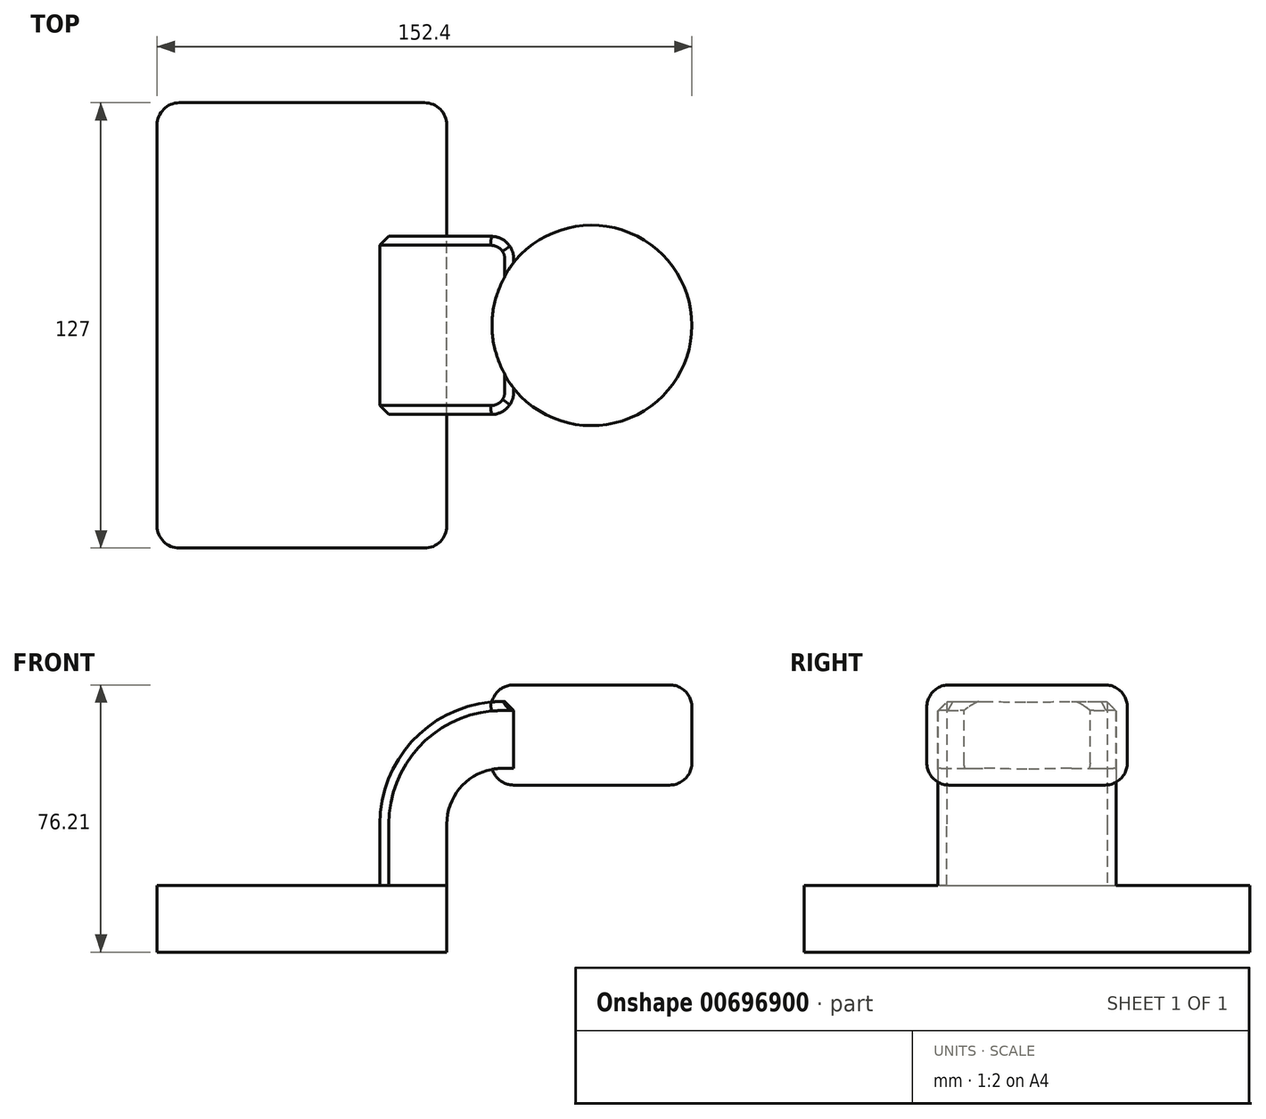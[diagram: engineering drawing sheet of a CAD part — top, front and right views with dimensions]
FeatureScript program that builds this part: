
annotation { "Feature Type Name" : "Feature", "Feature Type Description" : "" }
export const myFeature = defineFeature(function(context is Context, id is Id, definition is map)
    precondition{}
    {
        {
            var Q0;
            Q0=qCreatedBy(makeId("Front.planeOp"),FACE);
            var sketch = newSketch(context, id + "F0", { "sketchPlane" : qUnion([Q0])});
            skLineSegment(sketch, "E0.bottom", {"start": v(-41.28, 9.52) * mm, "end": v(41.27, 9.53) * mm});
            skLineSegment(sketch, "E0.top", {"start": v(-41.28, -9.52) * mm, "end": v(41.28, -9.52) * mm});
            skLineSegment(sketch, "E0.left", {"start": v(-41.28, 9.52) * mm, "end": v(-41.28, -9.53) * mm});
            skLineSegment(sketch, "E0.right", {"start": v(41.27, 9.53) * mm, "end": v(41.28, -9.52) * mm});
            skPoint(sketch, "E0.middle", {"position": v(0, 0) * mm});
            skLineSegment(sketch, "E1.bottom", {"start": v(111.12, 38.1) * mm, "end": v(60.32, 38.1) * mm});
            skLineSegment(sketch, "E1.top", {"start": v(111.12, 66.68) * mm, "end": v(60.32, 66.68) * mm});
            skLineSegment(sketch, "E1.left", {"start": v(111.12, 38.1) * mm, "end": v(111.12, 66.68) * mm});
            skLineSegment(sketch, "E1.right", {"start": v(60.32, 38.1) * mm, "end": v(60.32, 66.68) * mm});
            skPoint(sketch, "E1.middle", {"position": v(85.72, 52.39) * mm});
            skLineSegment(sketch, "E2", {"start": v(41.27, 9.53) * mm, "end": v(41.27, 27) * mm});
            skArc(sketch, "E3", {"start": v(41.27, 27) * mm, "mid": v(45.92, 38.23) * mm, "end": v(57.15, 42.88) * mm});
            skLineSegment(sketch, "E4", {"start": v(57.15, 42.88) * mm, "end": v(82.55, 42.88) * mm});
            skLineSegment(sketch, "E5.0", {"start": v(57.15, 61.93) * mm, "end": v(82.55, 61.93) * mm});
            skArc(sketch, "E5.1", {"start": v(22.22, 27) * mm, "mid": v(32.45, 51.7) * mm, "end": v(57.15, 61.93) * mm});
            skLineSegment(sketch, "E5.2", {"start": v(22.22, 9.53) * mm, "end": v(22.22, 27) * mm});
            skFitSpline(sketch, "E6", {"points": [v(-41.28, 9.52) * mm, v(57.15, 61.93) * mm], "startDerivative": vector(-0.04, 87.73) * mm, "endDerivative": vector(126.82, -4.98) * mm});
            skLineSegment(sketch, "E7", {"start": v(82.55, 66.68) * mm, "end": v(82.55, 38.1) * mm});
            skSolve(sketch);
        }
        {
            var Q0;
            Q0=makeQuery(id+"F0.imprint","IMPRINT",FACE,{"disambiguationData":[TD([[makeQuery(id+"F0.imprint","IMPRINT",EDGE,{"derivedFrom":sQuery(id+"F0.wireOp",EDGE,"E0.top")}),1.0]])]});
            extrude(context, id + "F1", {"entities" : qUnion([Q0]), "endBound" : BoundingType.SYMMETRIC, "depth" : 127 * mm, "offsetDistance" : 25.4 * mm});
        }
        {
            var Q0;
            {var subQ1=sQuery(id+"F0.wireOp",EDGE,"E2");Q0=makeQuery(id+"F0.imprint","IMPRINT",FACE,{"disambiguationData":[TD([[makeQuery(id+"F0.imprint","IMPRINT",EDGE,{"derivedFrom":subQ1}),1.0]])]});}
            extrude(context, id + "F2", {"entities" : qUnion([Q0]), "operationType" : NewBodyOperationType.ADD, "endBound" : BoundingType.SYMMETRIC, "depth" : 50.8 * mm, "offsetDistance" : 25.4 * mm});
        }
        {
            var Q0;
            Q0=makeQuery(id+"F0.imprint","IMPRINT",FACE,{"disambiguationData":[TD([[makeQuery(id+"F0.imprint","IMPRINT",EDGE,{"derivedFrom":sQuery(id+"F0.wireOp",EDGE,"E5.1")}),1.0]])]});
            extrude(context, id + "F3", {"entities" : qUnion([Q0]), "operationType" : NewBodyOperationType.ADD, "endBound" : BoundingType.SYMMETRIC, "depth" : 15.88 * mm, "offsetDistance" : 25.4 * mm});
        }
        {
            var Q0;
            {var subQ0=sQuery(id+"F0.wireOp",EDGE,"E1.left");Q0=makeQuery(id+"F0.imprint","IMPRINT",FACE,{"disambiguationData":[TD([[makeQuery(id+"F0.imprint","IMPRINT",EDGE,{"derivedFrom":subQ0}),1.0]])]});}
            var Q1;
            Q1=sQuery(id+"F0.wireOp",EDGE,"E7");
            revolve(context, id + "F4", {"operationType" : NewBodyOperationType.ADD, "entities" : qUnion([Q0]), "axis" : qUnion([Q1]), "revolveType" : RevolveType.FULL});
        }
        {
            var Q0;
            Q0=makeQuery(id+"F1.opExtrude","CAP_EDGE",EDGE,{"disambiguationData":[OSD([sQuery(id+"F0.wireOp",EDGE,"E0.right")])],"isStart":false});
            var Q1;
            Q1=makeQuery(id+"F1.opExtrude","CAP_EDGE",EDGE,{"disambiguationData":[OSD([sQuery(id+"F0.wireOp",EDGE,"E0.left")])],"isStart":false});
            var Q2;
            Q2=makeQuery(id+"F1.opExtrude","CAP_EDGE",EDGE,{"disambiguationData":[OSD([sQuery(id+"F0.wireOp",EDGE,"E0.right")])],"isStart":true});
            var Q3;
            Q3=makeQuery(id+"F1.opExtrude","CAP_EDGE",EDGE,{"disambiguationData":[OSD([sQuery(id+"F0.wireOp",EDGE,"E0.left")])],"isStart":true});
            var Q4;
            Q4=makeQuery(id+"F4.opRevolve","SWEPT_EDGE",EDGE,{"disambiguationData":[OSD([sQuery(id+"F0.wireOp",EDGE,"E1.top"),sQuery(id+"F0.wireOp",EDGE,"E1.left")])]});
            var Q5;
            Q5=makeQuery(id+"F4.opRevolve","SWEPT_EDGE",EDGE,{"disambiguationData":[OSD([sQuery(id+"F0.wireOp",EDGE,"E1.bottom"),sQuery(id+"F0.wireOp",EDGE,"E1.left")])]});
            var Q6;
            Q6=makeQuery(id+"F2.opExtrude","CAP_EDGE",EDGE,{"disambiguationData":[OSD([sQuery(id+"F0.wireOp",EDGE,"E1.right")])],"isStart":false});
            var Q7;
            Q7=makeQuery(id+"F2.opExtrude","CAP_EDGE",EDGE,{"disambiguationData":[OSD([sQuery(id+"F0.wireOp",EDGE,"E1.right")])],"isStart":true});
            fillet(context, id + "F5", {"entities" : qUnion([Q0, Q1, Q2, Q3, Q4, Q5, Q6, Q7]), "radius" : 6.35 * mm, "tangentPropagation" : true, "allowEdgeOverflow" : false});
        }
        {
            var Q0;
            Q0=makeQuery(id+"F3.opExtrude","CAP_EDGE",EDGE,{"disambiguationData":[OSD([sQuery(id+"F0.wireOp",EDGE,"E6")])],"isStart":false});
            var Q1;
            Q1=makeQuery(id+"F3.opExtrude","CAP_EDGE",EDGE,{"disambiguationData":[OSD([sQuery(id+"F0.wireOp",EDGE,"E6")])],"isStart":true});
            var Q2;
            Q2=makeQuery(id+"F2.opExtrude","CAP_EDGE",EDGE,{"disambiguationData":[OSD([sQuery(id+"F0.wireOp",EDGE,"E5.1")])],"isStart":false});
            var Q3;
            Q3=makeQuery(id+"F2.opExtrude","CAP_EDGE",EDGE,{"disambiguationData":[OSD([sQuery(id+"F0.wireOp",EDGE,"E5.1")])],"isStart":true});
            chamfer(context, id + "F6", {"entities" : qUnion([Q0, Q1, Q2, Q3]), "width" : 2.54 * mm, "tangentPropagation" : true});
        }
    });
